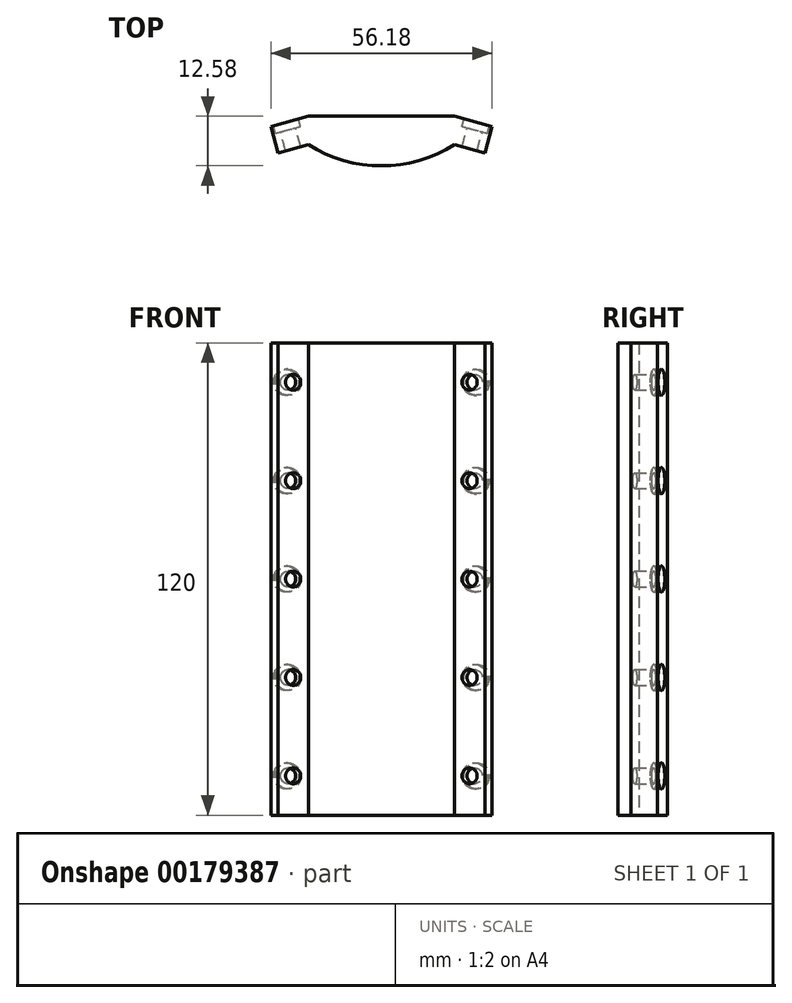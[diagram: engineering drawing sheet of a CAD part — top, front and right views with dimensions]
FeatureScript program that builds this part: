
annotation { "Feature Type Name" : "Feature", "Feature Type Description" : "" }
export const myFeature = defineFeature(function(context is Context, id is Id, definition is map)
    precondition{}
    {
        {
            var Q0;
            Q0=qCreatedBy(makeId("Top.planeOp"),FACE);
            var sketch = newSketch(context, id + "F0", { "sketchPlane" : qUnion([Q0])});
            skPoint(sketch, "E0.0", {"position": v(28.1, 4.88) * mm});
            skPoint(sketch, "E1.0", {"position": v(26.28, -1.88) * mm});
            skPoint(sketch, "E2.0", {"position": v(18.53, 0.2) * mm});
            skPoint(sketch, "E3.0", {"position": v(0, -5.14) * mm});
            skPoint(sketch, "E4.0", {"position": v(-18.53, 0.2) * mm});
            skPoint(sketch, "E5.0", {"position": v(-26.28, -1.88) * mm});
            skPoint(sketch, "E6.0", {"position": v(-28.1, 4.88) * mm});
            skLineSegment(sketch, "E7", {"start": v(-28.1, 4.88) * mm, "end": v(-26.28, -1.88) * mm});
            skLineSegment(sketch, "E8", {"start": v(-26.28, -1.88) * mm, "end": v(-18.53, 0.2) * mm});
            skLineSegment(sketch, "E9", {"start": v(28.1, 4.88) * mm, "end": v(26.28, -1.88) * mm});
            skLineSegment(sketch, "E10", {"start": v(26.28, -1.88) * mm, "end": v(18.53, 0.2) * mm});
            skPoint(sketch, "E11.0", {"position": v(23.96, 5.99) * mm});
            skPoint(sketch, "E12.0", {"position": v(-23.96, 5.99) * mm});
            skLineSegment(sketch, "E13", {"start": v(18.53, 0.2) * mm, "end": v(18.53, 9.46) * mm, "construction": true});
            skLineSegment(sketch, "E14", {"start": v(-18.53, 0.2) * mm, "end": v(-18.53, 9.3) * mm, "construction": true});
            skArc(sketch, "E15", {"start": v(-18.53, 0.2) * mm, "mid": v(0, -5.14) * mm, "end": v(18.53, 0.2) * mm});
            skLineSegment(sketch, "E16", {"start": v(28.1, 4.88) * mm, "end": v(18.53, 7.44) * mm});
            skLineSegment(sketch, "E17", {"start": v(-28.1, 4.88) * mm, "end": v(-18.53, 7.44) * mm});
            skLineSegment(sketch, "E18", {"start": v(-18.53, 7.44) * mm, "end": v(18.53, 7.44) * mm});
            skLineSegment(sketch, "E19", {"start": v(0, -5.14) * mm, "end": v(0, 7.44) * mm, "construction": true});
            skSolve(sketch);
        }
        {
            var Q0;
            Q0=makeQuery(id+"F0.imprint","IMPRINT",FACE,{"disambiguationData":[TD([[makeQuery(id+"F0.imprint","IMPRINT",EDGE,{"derivedFrom":sQuery(id+"F0.wireOp",EDGE,"fW5e1Rfe-XMRa-rqwH-YWug-YTGpKf2waGjB")}),-1.0]])]});
            var Q1;
            Q1=makeQuery(id+"F0.imprint","IMPRINT",FACE,{"disambiguationData":[TD([[makeQuery(id+"F0.imprint","IMPRINT",EDGE,{"derivedFrom":sQuery(id+"F0.wireOp",EDGE,"E7")}),1.0]])]});
            extrude(context, id + "F1", {"entities" : qUnion([Q0, Q1]), "depth" : 120 * mm});
        }
        {
            var Q0;
            Q0=makeQuery(id+"F1.opExtrude","SWEPT_FACE",FACE,{"disambiguationData":[OSD([sQuery(id+"F0.wireOp",EDGE,"E17")])]});
            var sketch = newSketch(context, id + "F2", { "sketchPlane" : qUnion([Q0])});
            skCircle(sketch, "E20.0", {"center": v(21.86, 10) * mm, "radius": 2.02 * mm});
            skLineSegment(sketch, "E21", {"start": v(21.86, 10) * mm, "end": v(21.86, 35) * mm, "construction": true});
            skLineSegment(sketch, "E22", {"start": v(21.86, 35) * mm, "end": v(21.86, 60) * mm, "construction": true});
            skLineSegment(sketch, "E23", {"start": v(21.86, 60) * mm, "end": v(21.86, 85) * mm, "construction": true});
            skLineSegment(sketch, "E24", {"start": v(21.86, 85) * mm, "end": v(21.86, 110) * mm, "construction": true});
            skSolve(sketch);
        }
        {
            var Q0;
            Q0=makeQuery(id+"F1.opExtrude","SWEPT_FACE",FACE,{"disambiguationData":[OSD([sQuery(id+"F0.wireOp",EDGE,"E16")])]});
            var sketch = newSketch(context, id + "F3", { "sketchPlane" : qUnion([Q0])});
            skCircle(sketch, "E25.0", {"center": v(-21.86, 10) * mm, "radius": 2.02 * mm});
            skLineSegment(sketch, "E26", {"start": v(-21.86, 10) * mm, "end": v(-21.86, 35) * mm, "construction": true});
            skLineSegment(sketch, "E27", {"start": v(-21.86, 35) * mm, "end": v(-21.86, 60) * mm, "construction": true});
            skLineSegment(sketch, "E28", {"start": v(-21.86, 60) * mm, "end": v(-21.86, 85) * mm, "construction": true});
            skLineSegment(sketch, "E29", {"start": v(-21.86, 85) * mm, "end": v(-21.86, 110) * mm, "construction": true});
            skSolve(sketch);
        }
        {
            var Q0;
            Q0=sQuery(id+"F3.wireOp",VERTEX,"E25.0.center");
            var Q1;
            Q1=sQuery(id+"F2.wireOp",VERTEX,"E20.0.center");
            var Q2;
            Q2=sQuery(id+"F2.wireOp",VERTEX,"E22.start");
            var Q3;
            Q3=sQuery(id+"F2.wireOp",VERTEX,"E23.start");
            var Q4;
            Q4=sQuery(id+"F2.wireOp",VERTEX,"E24.start");
            var Q5;
            Q5=sQuery(id+"F2.wireOp",VERTEX,"E24.end");
            var Q6;
            Q6=sQuery(id+"F3.wireOp",VERTEX,"E27.start");
            var Q7;
            Q7=sQuery(id+"F3.wireOp",VERTEX,"E28.start");
            var Q8;
            Q8=sQuery(id+"F3.wireOp",VERTEX,"E29.start");
            var Q9;
            Q9=sQuery(id+"F3.wireOp",VERTEX,"E29.end");
            var Q10;
            Q10=makeQuery(id+"F1.opExtrude","SWEPT_BODY",BODY,{"disambiguationData":[OSD([sQuery(id+"F0.wireOp",EDGE,"E7"),sQuery(id+"F0.wireOp",EDGE,"E8"),sQuery(id+"F0.wireOp",EDGE,"E9"),sQuery(id+"F0.wireOp",EDGE,"E10"),sQuery(id+"F0.wireOp",EDGE,"E15"),sQuery(id+"F0.wireOp",EDGE,"E16"),sQuery(id+"F0.wireOp",EDGE,"E17"),sQuery(id+"F0.wireOp",EDGE,"E18")])]});
            hole(context, id + "F4", {"style" : HoleStyle.C_BORE, "endStyle" : HoleEndStyle.THROUGH, "holeDiameter" : 4 * mm, "cBoreDiameter" : 6.65 * mm, "cBoreDepth" : 2 * mm, "locations" : qUnion([Q0, Q1, Q2, Q3, Q4, Q5, Q6, Q7, Q8, Q9]), "scope" : qUnion([Q10]), "tappedDepth" : 12 * mm, "tapClearance" : 3});
        }
    });
